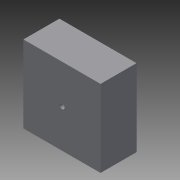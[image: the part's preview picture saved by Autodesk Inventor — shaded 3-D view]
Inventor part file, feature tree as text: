
AUTODESK INVENTOR PART (.ipt)
format: ipt  version: 2014 (Build 180170000, 170)  size: 2,039,296 bytes
history: native  units: mm
features: sketch x38, plane x28, fillet x17, extrude x14, chamfer x4, other x3, loft x1, mirror x1, move_body x1, boolean_combine x1
ambient origin geometry x8: Origin, YZ Plane, XZ Plane, XY Plane, X Axis, Y Axis, Z Axis, Center Point
bodies: Solid1 (feature_tree), Solid2 (feature_tree)
feature tree (108):
  other  "Part5.ipt"
  sketch  "Sketch1"  dims[d1=8.0mm d2=7.0mm]
  plane  "Work Plane4"
  sketch  "Sketch2"  dims[d3=7.0mm d4=8.0mm d8=20.0mm d9=-3.490659mm d11=8.0mm d12=8.0mm d14=2.0mm d15=10.0mm d17=-1.745329mm d18=1.0mm d19=11.75mm]
  sketch  "Sketch3"  dims[d20=20.0mm d21=9.5mm]
  sketch  "Sketch4"  dims[d22=8.0mm d23=0.0mm d25=9.0mm]
  sketch  "Sketch5"  dims[d27=8.5mm d28=3.0mm]
  sketch  "Sketch6"  dims[d29=-1.745329mm d30=-3.490659mm d31=1.0mm d32=2.0mm d33=8.6mm]
  plane  "Work Plane5"
  sketch  "Sketch7"  dims[d34=8.5mm d35=7.0mm]
  plane  "Work Plane7"
  sketch  "Sketch8"  dims[d36=7.0mm d37=5.0mm d38=3.0mm]
  plane  "Work Plane8"
  sketch  "Sketch9"  dims[d39=17.0mm]
  plane  "Work Plane10"
  sketch  "Sketch10"  dims[d40=8.0mm]
  plane  "Work Plane11"
  plane  "Work Plane12"
  sketch  "Sketch11"  dims[d41=17.0mm]
  sketch  "Sketch12"  dims[d42=7.7mm]
  sketch  "Sketch13"  dims[d43=17.0mm]
  plane  "Work Plane13"
  plane  "Work Plane14"
  plane  "Work Plane15"
  plane  "Work Plane16"
  sketch  "Sketch14"  dims[d44=6.8mm]
  sketch  "Sketch15"  dims[d45=17.0mm]
  plane  "Work Plane20"
  sketch  "Sketch16"  dims[d46=5.0mm]
  sketch  "Sketch17"  dims[d47=2.0mm]
  sketch  "Sketch18"  dims[d48=17.0mm]
  sketch  "Sketch19"  dims[d49=2.0mm]
  plane  "Work Plane21"
  loft  "Loft1"
  extrude  "Extrusion1"  Depth=1.0mm
  fillet  "Fillet1"  [1 undecoded]
  fillet  "Fillet2"  Radius=8.0mm
  fillet  "Fillet3"  Radius=2.0mm
  fillet  "Fillet4"  Radius=10.0mm
  fillet  "Fillet5"  Radius=1.0mm
  fillet  "Fillet6"  Radius=11.75mm
  plane  "Work Plane23"
  plane  "Work Plane25"
  sketch  "Sketch22"  dims[d81=0.0mm d82=90.0deg d83=0.0mm d84=90.0deg]
  extrude  "Extrusion2"  Depth=9.5mm
  plane  "Work Plane26"
  sketch  "Sketch24"  dims[d86=6.0mm]
  sketch  "Sketch25"  dims[d87=6.0mm]
  extrude  "Extrusion3"  Depth=9.0mm
  extrude  "Extrusion4"  Depth=3.0mm
  sketch  "Sketch27"  dims[d89=135.0deg]
  extrude  "Extrusion5"  Depth=1.0mm
  sketch  "Sketch29"  dims[d91=45.0deg d92=15.0mm d93=0.0mm]
  extrude  "Extrusion6"  Depth=7.0mm
  extrude  "Extrusion7"  Depth=5.0mm
  mirror  "Mirror1"
  chamfer  "Chamfer1"  Angle=90.0deg  [1 undecoded]
  fillet  "Fillet7"  [1 undecoded]
  fillet  "Fillet8"  [1 undecoded]
  fillet  "Fillet9"  [1 undecoded]
  fillet  "Fillet10"  [1 undecoded]
  fillet  "Fillet11"  [1 undecoded]
  chamfer  "Chamfer2"  Angle=90.0deg  [1 undecoded]
  fillet  "Fillet12"  [1 undecoded]
  fillet  "Fillet13"  [1 undecoded]
  fillet  "Fillet14"  [1 undecoded]
  fillet  "Fillet15"  [1 undecoded]
  fillet  "Fillet16"  [1 undecoded]
  fillet  "Fillet17"  [1 undecoded]
  sketch  "Sketch31"  dims[d96=2.0mm d97=2.0mm]
  plane  "Work Plane27"
  extrude  "Extrusion9"  TaperAngle=0.0deg  [1 undecoded]
  extrude  "Extrusion10"  TaperAngle=0.0deg  [1 undecoded]
  chamfer  "Chamfer4"  Distance=15.0mm
  extrude  "Extrusion11"  Depth=2.0mm
  extrude  "Extrusion12"  Depth=2.0mm
  extrude  "Extrusion13"  Depth=2.0mm
  chamfer  "Chamfer5"  Distance=22.0mm Angle=90.0deg
  plane  "Work Plane28"
  move_body  "Move Body1"
  boolean_combine  "Combine1"
  extrude  "Extrusion15"  Depth=3.0mm
  extrude  "Extrusion16"  Depth=8.0mm
  plane  "Work Plane1"
  plane  "Work Plane2"
  plane  "Work Plane3"
  plane  "Work Plane6"
  plane  "Work Plane9"
  plane  "Work Plane17"
  plane  "Work Plane18"
  plane  "Work Plane19"
  sketch  "Sketch20"  dims[d50=2.0mm d51=0.0mm d52=90.0deg d53=0.0mm d54=90.0deg d55=0.0mm d56=90.0deg d57=0.0mm d58=90.0deg d59=0.0mm d60=90.0deg d61=0.0mm d62=90.0deg d63=0.0mm d64=90.0deg d65=0.0mm d66=90.0deg d67=0.0mm d68=90.0deg d69=0.0mm d70=90.0deg d71=0.0mm d72=90.0deg d73=0.0mm d74=90.0deg d75=0.0mm d76=90.0deg]
  sketch  "Sketch21"  dims[d77=0.0mm d78=90.0deg d79=0.0mm d80=90.0deg]
  plane  "Work Plane22"
  plane  "Work Plane24"
  sketch  "Sketch23"  dims[d85=0.3mm]
  sketch  "Sketch26"  dims[d88=2.0mm]
  sketch  "Sketch28"  dims[d90=2.0mm]
  sketch  "Sketch30"  dims[d94=2.0mm d95=2.0mm]
  sketch  "Sketch32"  dims[d98=2.0mm d99=2.0mm d100=90.0deg d101=22.0mm]
  sketch  "Sketch33"  dims[d102=12.217305mm d103=20.0mm d110=3.0mm]
  sketch  "Sketch34"  dims[d111=6.0mm d112=8.0mm]
  sketch  "Sketch35"  dims[d113=6.0mm]
  sketch  "Sketch36"  dims[d114=20.0mm d115=0.0mm]
  other  "Solid1::Part5.ipt"
  other  "TaggingFeature1"
  sketch  "Sketch38"  dims[d116=12.0mm]
  sketch  "Sketch39"  dims[d117=20.0mm d118=10.0mm d123=2.0mm d124=4.0mm d125=4.0mm d126=12.0mm d127=6.0mm d128=6.0mm d129=0.0mm d130=10.75mm d131=9.0mm d132=9.0mm d133=60.0mm d134=0.0mm d135=30.0mm d136=2.0mm d137=12.0mm d138=6.0mm d139=0.0mm d140=1.2mm d141=8.0mm d142=8.0mm d143=1.2mm d144=12.0mm d145=0.0mm d146=20.0mm d147=0.0mm d148=0.5mm d149=2.0mm d150=45.0deg d151=1.0mm d152=0.5mm d153=0.5mm d154=1.0mm d155=0.5mm d156=0.5mm d157=2.0mm d158=45.0deg d159=1.0mm d160=0.5mm d161=1.0mm d162=0.5mm d163=0.5mm d164=0.5mm d167=4.2mm d168=0.0mm d172=4.5mm d173=2.7mm d174=0.0mm d175=2.0mm d176=2.0mm d177=45.0deg d178=2.8mm d179=0.0mm d180=14.0mm d181=4.2mm d182=0.0mm d183=2.8mm d184=0.0mm d185=2.0mm d186=2.0mm d187=45.0deg d188=60.0deg d194=10.0mm d195=87.0mm d196=-61.0mm d197=-15.0mm d198=16.0mm d199=0.0mm d200=2.0mm d201=30.0mm d202=0.0mm]
note: 16 required parameter values undecoded (feature->parameter linkage not recoverable at this tier; creation-order binding heuristic only, values carry confidence <= 0.55)
